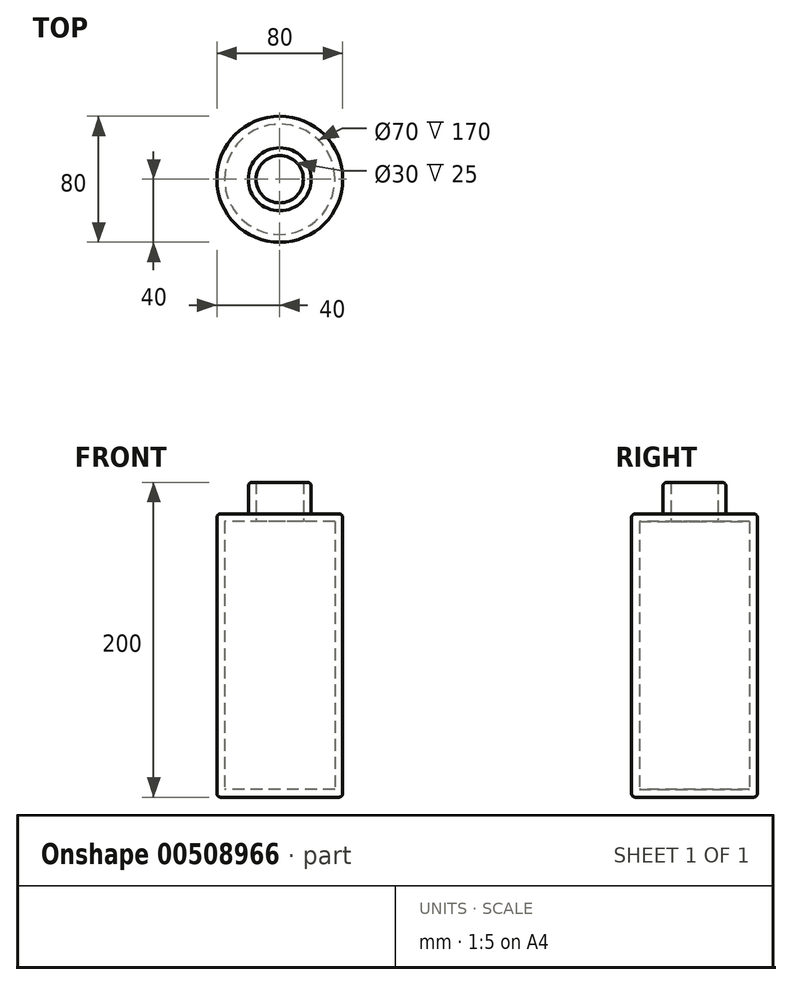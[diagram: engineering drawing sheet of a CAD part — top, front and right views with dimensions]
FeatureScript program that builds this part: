
annotation { "Feature Type Name" : "Feature", "Feature Type Description" : "" }
export const myFeature = defineFeature(function(context is Context, id is Id, definition is map)
    precondition{}
    {
        {
            var Q0;
            Q0=qCreatedBy(makeId("Top.planeOp"),FACE);
            var sketch = newSketch(context, id + "F0", { "sketchPlane" : qUnion([Q0])});
            skCircle(sketch, "E0", {"center": v(0, 0) * mm, "radius": 40 * mm});
            skSolve(sketch);
        }
        {
            var Q0;
            Q0=makeQuery(id+"F0.imprint","IMPRINT",FACE,{"disambiguationData":[TD([[makeQuery(id+"F0.imprint","IMPRINT",EDGE,{"derivedFrom":sQuery(id+"F0.wireOp",EDGE,"E0")}),1.0]])]});
            extrude(context, id + "F1", {"entities" : qUnion([Q0]), "depth" : 180 * mm});
        }
        {
            var Q0;
            Q0=makeQuery(id+"F1.opExtrude","CAP_FACE",FACE,{"disambiguationData":[OSD([sQuery(id+"F0.wireOp",EDGE,"E0")])],"isStart":false});
            var sketch = newSketch(context, id + "F2", { "sketchPlane" : qUnion([Q0])});
            skCircle(sketch, "E1", {"center": v(0, 0) * mm, "radius": 20 * mm});
            skSolve(sketch);
        }
        {
            var Q0;
            Q0=makeQuery(id+"F2.imprint","IMPRINT",FACE,{"disambiguationData":[TD([[makeQuery(id+"F2.imprint","IMPRINT",EDGE,{"derivedFrom":sQuery(id+"F2.wireOp",EDGE,"E1")}),1.0]])]});
            extrude(context, id + "F3", {"entities" : qUnion([Q0]), "operationType" : NewBodyOperationType.ADD, "depth" : 20 * mm});
        }
        {
            var Q0;
            Q0=makeQuery(id+"F3.opExtrude","CAP_EDGE",EDGE,{"disambiguationData":[OSD([sQuery(id+"F2.wireOp",EDGE,"E1")])],"isStart":false});
            var Q1;
            Q1=makeQuery(id+"F1.opExtrude","CAP_EDGE",EDGE,{"disambiguationData":[OSD([sQuery(id+"F0.wireOp",EDGE,"E0")])],"isStart":false});
            var Q2;
            Q2=makeQuery(id+"F1.opExtrude","CAP_EDGE",EDGE,{"disambiguationData":[OSD([sQuery(id+"F0.wireOp",EDGE,"E0")])],"isStart":true});
            fillet(context, id + "F4", {"entities" : qUnion([Q0, Q1, Q2]), "radius" : 2.5 * mm, "tangentPropagation" : true, "allowEdgeOverflow" : false});
        }
        {
            var Q0;
            Q0=makeQuery(id+"F3.opExtrude","CAP_FACE",FACE,{"disambiguationData":[OSD([sQuery(id+"F2.wireOp",EDGE,"E1")])],"isStart":false});
            shell(context, id + "F5", {"entities" : qUnion([Q0]), "thickness" : 5 * mm});
        }
    });
